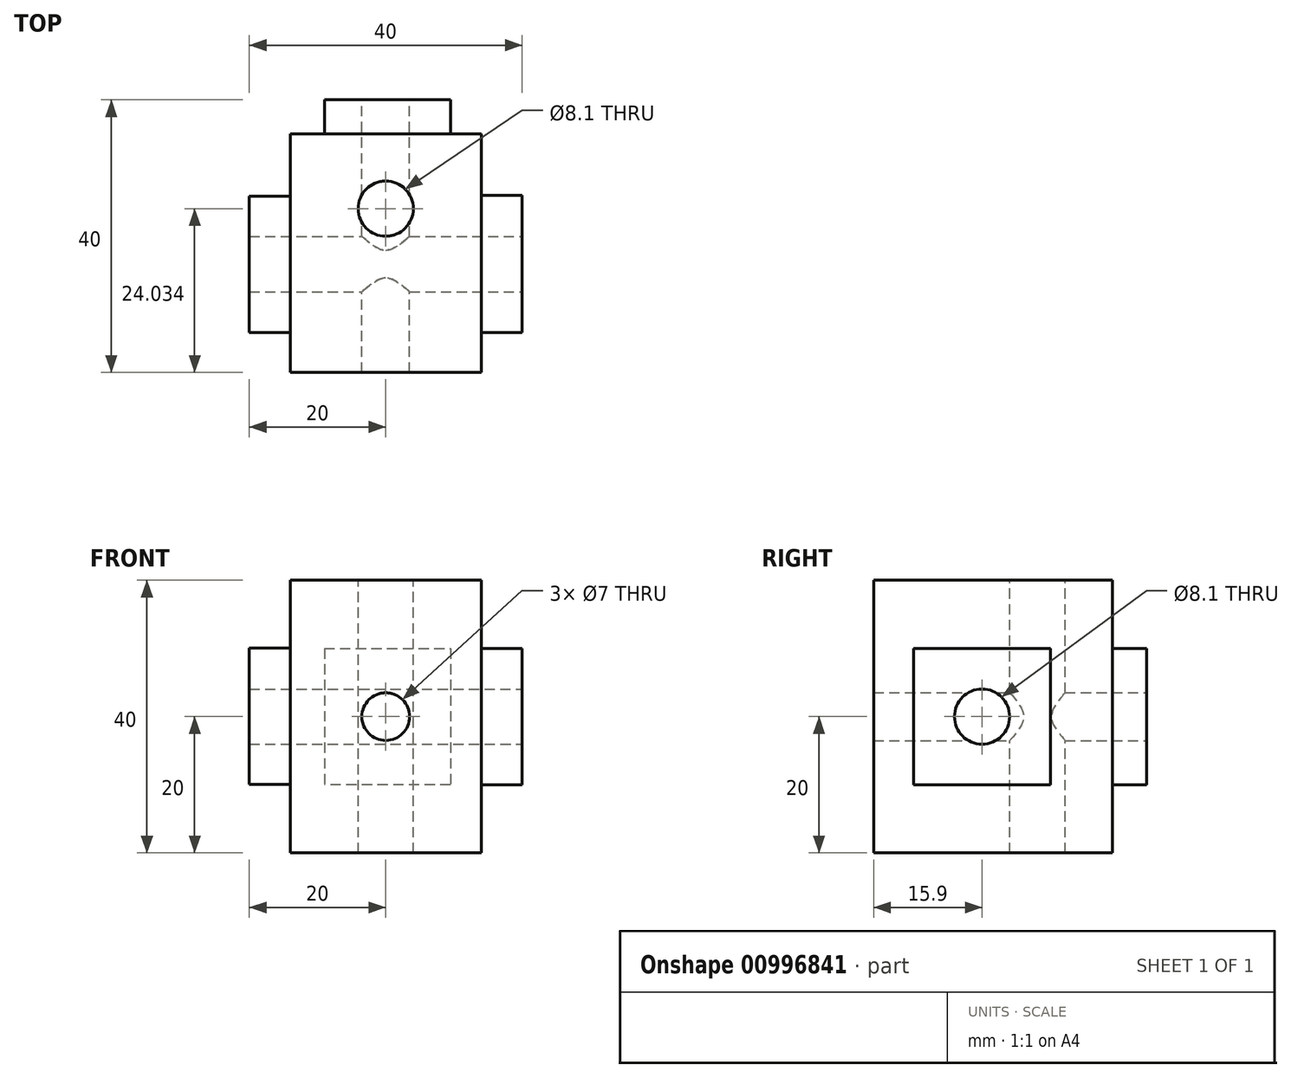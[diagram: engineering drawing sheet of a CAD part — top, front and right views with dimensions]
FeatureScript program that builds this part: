
annotation { "Feature Type Name" : "Feature", "Feature Type Description" : "" }
export const myFeature = defineFeature(function(context is Context, id is Id, definition is map)
    precondition{}
    {
        {
            var Q0;
            Q0=qCreatedBy(makeId("Top.planeOp"),FACE);
            var sketch = newSketch(context, id + "F0", { "sketchPlane" : qUnion([Q0])});
            skLineSegment(sketch, "E0.bottom", {"start": v(20, -20) * mm, "end": v(-20, -20) * mm});
            skLineSegment(sketch, "E0.top", {"start": v(20, 20) * mm, "end": v(-20, 20) * mm});
            skLineSegment(sketch, "E0.left", {"start": v(20, -20) * mm, "end": v(20, 20) * mm});
            skLineSegment(sketch, "E0.right", {"start": v(-20, -20) * mm, "end": v(-20, 20) * mm});
            skPoint(sketch, "E0.middle", {"position": v(0, 0) * mm});
            skSolve(sketch);
        }
        {
            var Q0;
            Q0=makeQuery(id+"F0.imprint","IMPRINT",FACE,{"disambiguationData":[TD([[makeQuery(id+"F0.imprint","IMPRINT",EDGE,{"derivedFrom":sQuery(id+"F0.wireOp",EDGE,"E0.bottom")}),-1.0]])]});
            extrude(context, id + "F1", {"entities" : qUnion([Q0]), "depth" : 40 * mm, "offsetDistance" : 25 * mm});
        }
        {
            var Q0;
            Q0=makeQuery(id+"F1.opExtrude","CAP_FACE",FACE,{"disambiguationData":[OSD([sQuery(id+"F0.wireOp",EDGE,"E0.bottom"),sQuery(id+"F0.wireOp",EDGE,"E0.top"),sQuery(id+"F0.wireOp",EDGE,"E0.left"),sQuery(id+"F0.wireOp",EDGE,"E0.right")])],"isStart":false});
            var sketch = newSketch(context, id + "F2", { "sketchPlane" : qUnion([Q0])});
            skCircle(sketch, "E1", {"center": v(0, 4.03) * mm, "radius": 4.05 * mm});
            skSolve(sketch);
        }
        {
            var Q0;
            Q0=makeQuery(id+"F2.imprint","IMPRINT",FACE,{"disambiguationData":[TD([[makeQuery(id+"F2.imprint","IMPRINT",EDGE,{"derivedFrom":sQuery(id+"F2.wireOp",EDGE,"E1")}),1.0]])]});
            extrude(context, id + "F3", {"entities" : qUnion([Q0]), "operationType" : NewBodyOperationType.REMOVE, "oppositeDirection" : true, "depth" : 40 * mm, "offsetDistance" : 25 * mm});
        }
        {
            var Q0;
            Q0=makeQuery(id+"F1.opExtrude","SWEPT_FACE",FACE,{"disambiguationData":[OSD([sQuery(id+"F0.wireOp",EDGE,"E0.left")])]});
            var sketch = newSketch(context, id + "F4", { "sketchPlane" : qUnion([Q0])});
            skCircle(sketch, "E2", {"center": v(-4.1, 20) * mm, "radius": 4.05 * mm});
            skSolve(sketch);
        }
        {
            var Q0;
            Q0=makeQuery(id+"F4.imprint","IMPRINT",FACE,{"disambiguationData":[TD([[makeQuery(id+"F4.imprint","IMPRINT",EDGE,{"derivedFrom":sQuery(id+"F4.wireOp",EDGE,"E2")}),1.0]])]});
            extrude(context, id + "F5", {"entities" : qUnion([Q0]), "operationType" : NewBodyOperationType.REMOVE, "oppositeDirection" : true, "depth" : 40 * mm, "offsetDistance" : 25 * mm});
        }
        {
            var Q0;
            Q0=makeQuery(id+"F1.opExtrude","SWEPT_FACE",FACE,{"disambiguationData":[OSD([sQuery(id+"F0.wireOp",EDGE,"E0.top")])]});
            var sketch = newSketch(context, id + "F6", { "sketchPlane" : qUnion([Q0])});
            skCircle(sketch, "E3", {"center": v(0, 20) * mm, "radius": 3.5 * mm});
            skSolve(sketch);
        }
        {
            var Q0;
            Q0=makeQuery(id+"F6.imprint","IMPRINT",FACE,{"disambiguationData":[TD([[makeQuery(id+"F6.imprint","IMPRINT",EDGE,{"derivedFrom":sQuery(id+"F6.wireOp",EDGE,"E3")}),1.0]])]});
            extrude(context, id + "F7", {"entities" : qUnion([Q0]), "operationType" : NewBodyOperationType.REMOVE, "oppositeDirection" : true, "depth" : 40 * mm, "offsetDistance" : 25 * mm});
        }
        {
            var Q0;
            Q0=makeQuery(id+"F1.opExtrude","SWEPT_FACE",FACE,{"disambiguationData":[OSD([sQuery(id+"F0.wireOp",EDGE,"E0.left")])]});
            var sketch = newSketch(context, id + "F8", { "sketchPlane" : qUnion([Q0])});
            skLineSegment(sketch, "E4", {"start": v(-20, 20) * mm, "end": v(20, 20) * mm, "construction": true});
            skLineSegment(sketch, "E5", {"start": v(-14.15, 30) * mm, "end": v(5.95, 30) * mm});
            skLineSegment(sketch, "E6", {"start": v(-14.15, 10) * mm, "end": v(5.95, 10) * mm});
            skLineSegment(sketch, "E7", {"start": v(5.95, 30) * mm, "end": v(5.95, 10) * mm});
            skPoint(sketch, "E8.orphan", {"position": v(5.95, 0) * mm});
            skLineSegment(sketch, "E9", {"start": v(8.08, 40) * mm, "end": v(8.08, 0) * mm, "construction": true});
            skLineSegment(sketch, "E10", {"start": v(-14.15, 30) * mm, "end": v(-14.15, 10) * mm});
            skSolve(sketch);
        }
        {
            var Q0;
            {var subQ2=sQuery(id+"F8.wireOp",EDGE,"E5");Q0=makeQuery(id+"F8.imprint","IMPRINT",FACE,{"disambiguationData":[TD([[makeQuery(id+"F8.imprint","IMPRINT",EDGE,{"derivedFrom":subQ2}),1.0]])]});}
            extrude(context, id + "F9", {"entities" : qUnion([Q0]), "operationType" : NewBodyOperationType.REMOVE, "oppositeDirection" : true, "depth" : 6 * mm, "offsetDistance" : 25 * mm});
        }
        {
            var Q0;
            Q0=makeQuery(id+"F1.opExtrude","SWEPT_FACE",FACE,{"disambiguationData":[OSD([sQuery(id+"F0.wireOp",EDGE,"E0.top")])]});
            var sketch = newSketch(context, id + "F10", { "sketchPlane" : qUnion([Q0])});
            skLineSegment(sketch, "E11", {"start": v(-14, 20) * mm, "end": v(20, 20) * mm, "construction": true});
            skLineSegment(sketch, "E12", {"start": v(9, 30) * mm, "end": v(-9.5, 30) * mm});
            skLineSegment(sketch, "E13", {"start": v(-9.5, 30) * mm, "end": v(-9.5, 10) * mm});
            skLineSegment(sketch, "E14", {"start": v(-9.5, 10) * mm, "end": v(9, 10) * mm});
            skLineSegment(sketch, "E15", {"start": v(9, 30) * mm, "end": v(9, 10) * mm});
            skPoint(sketch, "E16.orphan", {"position": v(20, 10) * mm});
            skSolve(sketch);
        }
        {
            var Q0;
            {var subQ2=sQuery(id+"F10.wireOp",EDGE,"E12");Q0=makeQuery(id+"F10.imprint","IMPRINT",FACE,{"disambiguationData":[TD([[makeQuery(id+"F10.imprint","IMPRINT",EDGE,{"derivedFrom":subQ2}),-1.0]])]});}
            var Q1;
            {var subQ1=sQuery(id+"F0.wireOp",EDGE,"E0.top");var subQ6=makeQuery(id+"F1.opExtrude","CAP_EDGE",EDGE,{"disambiguationData":[OSD([subQ1])],"isStart":true});Q1=makeQuery(id+"F10.imprint","IMPRINT",FACE,{"disambiguationData":[TD([[makeQuery(id+"F10.imprint","IMPRINT",EDGE,{"derivedFrom":subQ6}),1.0]])]});}
            extrude(context, id + "F11", {"entities" : qUnion([Q0, Q1]), "operationType" : NewBodyOperationType.REMOVE, "oppositeDirection" : true, "depth" : 5 * mm, "offsetDistance" : 25 * mm});
        }
        {
            var Q0;
            Q0=makeQuery(id+"F1.opExtrude","SWEPT_FACE",FACE,{"disambiguationData":[OSD([sQuery(id+"F0.wireOp",EDGE,"E0.right")])]});
            var sketch = newSketch(context, id + "F12", { "sketchPlane" : qUnion([Q0])});
            skLineSegment(sketch, "E17", {"start": v(-15, 20) * mm, "end": v(20, 20) * mm, "construction": true});
            skLineSegment(sketch, "E18.bottom", {"start": v(-5.85, 30.07) * mm, "end": v(14.15, 30.07) * mm});
            skLineSegment(sketch, "E18.top", {"start": v(-5.85, 10.07) * mm, "end": v(14.15, 10.07) * mm});
            skLineSegment(sketch, "E18.left", {"start": v(-5.85, 30.07) * mm, "end": v(-5.85, 10.07) * mm});
            skLineSegment(sketch, "E18.right", {"start": v(14.15, 30.07) * mm, "end": v(14.15, 10.07) * mm});
            skSolve(sketch);
        }
        {
            var Q0;
            Q0=makeQuery(id+"F12.imprint","IMPRINT",FACE,{"disambiguationData":[TD([[makeQuery(id+"F12.imprint","IMPRINT",EDGE,{"derivedFrom":sQuery(id+"F12.wireOp",EDGE,"E18.bottom")}),1.0]])]});
            extrude(context, id + "F13", {"entities" : qUnion([Q0]), "operationType" : NewBodyOperationType.REMOVE, "oppositeDirection" : true, "depth" : 6 * mm, "offsetDistance" : 25 * mm});
        }
    });
